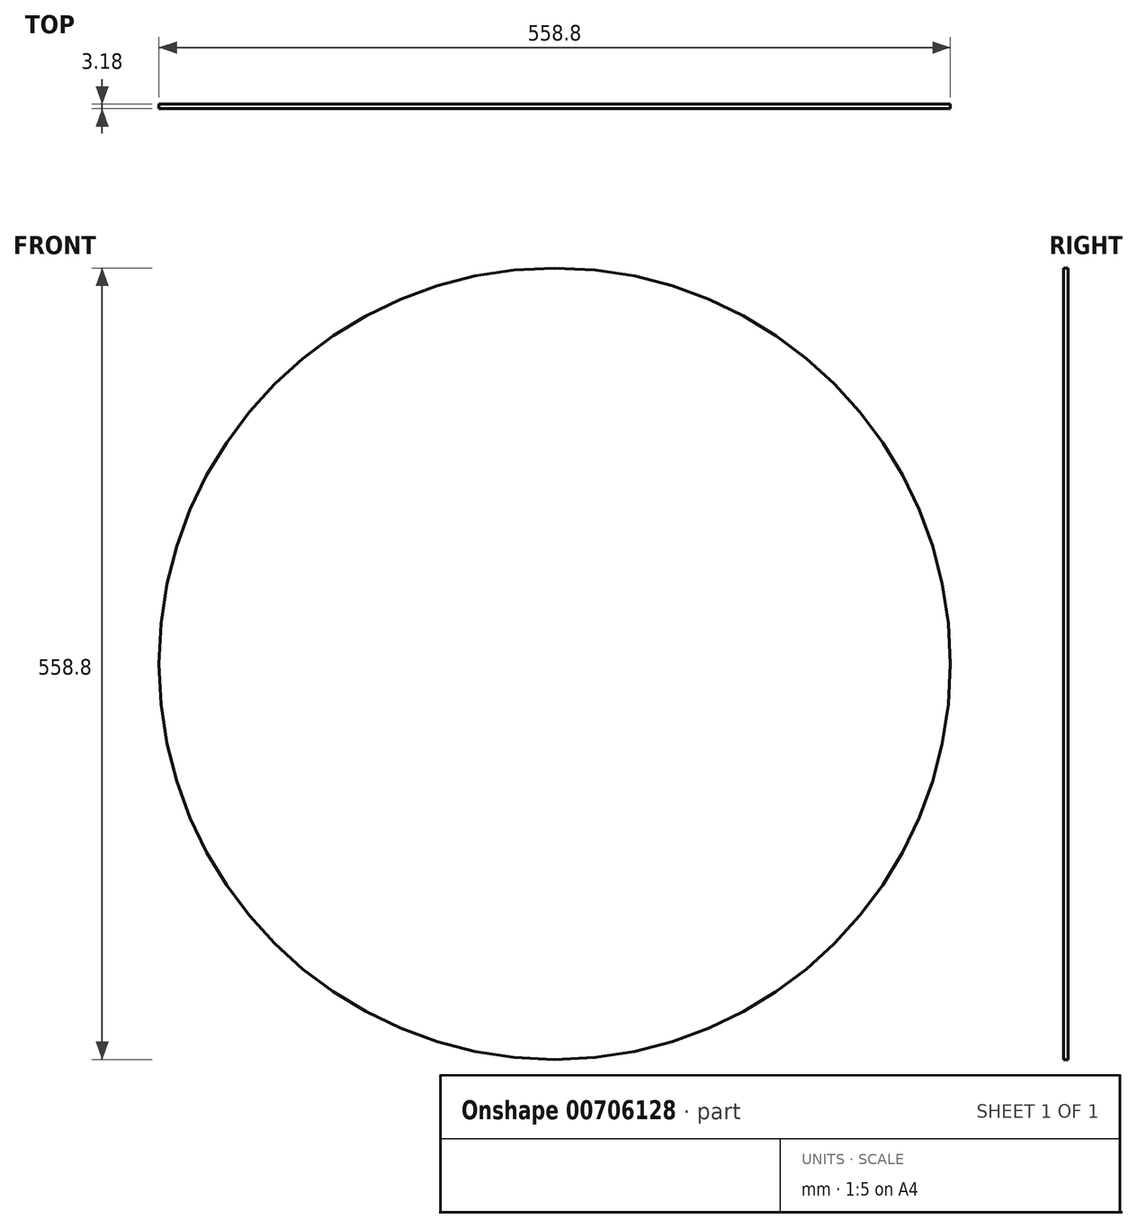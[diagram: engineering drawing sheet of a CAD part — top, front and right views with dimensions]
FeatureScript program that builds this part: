
annotation { "Feature Type Name" : "Feature", "Feature Type Description" : "" }
export const myFeature = defineFeature(function(context is Context, id is Id, definition is map)
    precondition{}
    {
        {
            var Q0;
            Q0=qCreatedBy(makeId("Front.planeOp"),FACE);
            var sketch = newSketch(context, id + "F0", { "sketchPlane" : qUnion([Q0])});
            skCircle(sketch, "E0", {"center": v(0, 0) * mm, "radius": 279.4 * mm});
            skSolve(sketch);
        }
        {
            var Q0;
            Q0=makeQuery(id+"F0.imprint","IMPRINT",FACE,{"disambiguationData":[TD([[makeQuery(id+"F0.imprint","IMPRINT",EDGE,{"derivedFrom":sQuery(id+"F0.wireOp",EDGE,"E0")}),1.0]])]});
            extrude(context, id + "F1", {"entities" : qUnion([Q0]), "depth" : 3.17 * mm, "offsetDistance" : 25.4 * mm});
        }
    });
